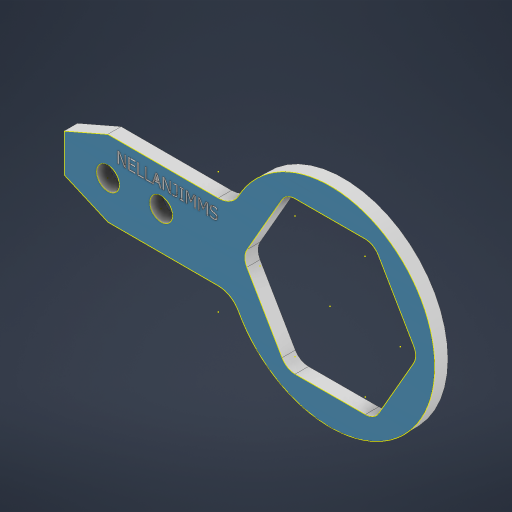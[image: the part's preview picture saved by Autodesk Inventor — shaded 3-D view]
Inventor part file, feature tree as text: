
AUTODESK INVENTOR PART (.ipt)
format: ipt  version: 2023 (Build 270158000, 158)  size: 390,656 bytes
history: native  units: mm
features: sketch x3, extrude x1, emboss x1, projected_geometry x1
ambient origin geometry x8: Origin, YZ Plane, XZ Plane, XY Plane, X Axis, Y Axis, Z Axis, Center Point
bodies: Solid1 (feature_tree)
feature tree (6):
  extrude  "Extrusion1"  Depth=80.0mm
  sketch  "Sketch2"  dims[d3=110.0mm]
  emboss  "Emboss1"
  sketch  "Sketch1"  dims[d1=79.999771mm d2=80.0mm]
  projected_geometry  "Projected Loop1"
  sketch  "Sketch3"  dims[d4=20.0mm d5=140.0mm d6=40.0mm d10=12.0mm d11=8.0mm d12=12.0mm d13=23.0mm d14=28.0mm d15=7.0mm d16=0.0mm d17=2.0mm d18=0.0mm]
